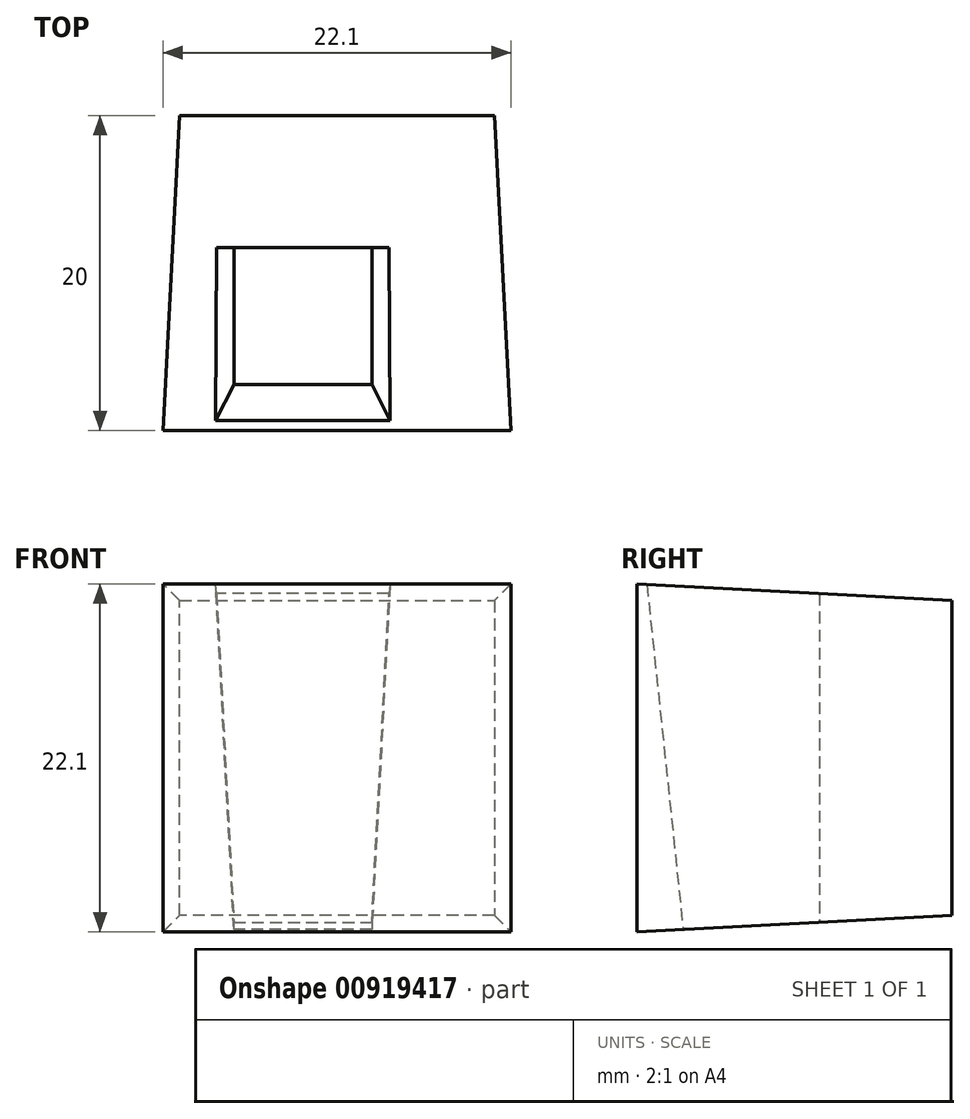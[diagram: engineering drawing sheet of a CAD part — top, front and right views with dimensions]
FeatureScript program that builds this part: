
annotation { "Feature Type Name" : "Feature", "Feature Type Description" : "" }
export const myFeature = defineFeature(function(context is Context, id is Id, definition is map)
    precondition{}
    {
        {
            var Q0;
            Q0=qCreatedBy(makeId("Front.planeOp"),FACE);
            var sketch = newSketch(context, id + "F0", { "sketchPlane" : qUnion([Q0])});
            skLineSegment(sketch, "E0.bottom", {"start": v(-10, 10) * mm, "end": v(10, 10) * mm});
            skLineSegment(sketch, "E0.top", {"start": v(-10, -10) * mm, "end": v(10, -10) * mm});
            skLineSegment(sketch, "E0.left", {"start": v(-10, 10) * mm, "end": v(-10, -10) * mm});
            skLineSegment(sketch, "E0.right", {"start": v(10, 10) * mm, "end": v(10, -10) * mm});
            skPoint(sketch, "E1", {"position": v(-10, 0) * mm});
            skPoint(sketch, "E2", {"position": v(0, 10) * mm});
            skSolve(sketch);
        }
        {
            var Q0;
            Q0=makeQuery(id+"F0.imprint","IMPRINT",FACE,{"disambiguationData":[TD([[makeQuery(id+"F0.imprint","IMPRINT",EDGE,{"derivedFrom":sQuery(id+"F0.wireOp",EDGE,"E0.bottom")}),-1.0]])]});
            extrude(context, id + "F1", {"entities" : qUnion([Q0]), "depth" : 20 * mm, "offsetDistance" : 25.4 * mm, "hasDraft" : true, "draftAngle" : 3 * degree});
        }
        {
            var Q0;
            Q0=makeQuery(id+"F1.opExtrude","SWEPT_FACE",FACE,{"disambiguationData":[OSD([sQuery(id+"F0.wireOp",EDGE,"E0.top")])]});
            var sketch = newSketch(context, id + "F2", { "sketchPlane" : qUnion([Q0])});
            skLineSegment(sketch, "E3.bottom", {"start": v(2.2, 8.93) * mm, "end": v(-6.55, 8.93) * mm});
            skLineSegment(sketch, "E3.top", {"start": v(2.2, 17.61) * mm, "end": v(-6.55, 17.61) * mm});
            skLineSegment(sketch, "E3.left", {"start": v(2.2, 8.93) * mm, "end": v(2.2, 17.61) * mm});
            skLineSegment(sketch, "E3.right", {"start": v(-6.55, 8.93) * mm, "end": v(-6.55, 17.61) * mm});
            skPoint(sketch, "E3.middle", {"position": v(-2.17, 13.27) * mm});
            skSolve(sketch);
        }
        {
            var Q0;
            Q0=makeQuery(id+"F2.imprint","IMPRINT",FACE,{"disambiguationData":[TD([[makeQuery(id+"F2.imprint","IMPRINT",EDGE,{"derivedFrom":sQuery(id+"F2.wireOp",EDGE,"E3.bottom")}),-1.0]])]});
            extrude(context, id + "F3", {"entities" : qUnion([Q0]), "operationType" : NewBodyOperationType.REMOVE, "endBound" : BoundingType.THROUGH_ALL, "oppositeDirection" : true, "depth" : 10 * mm, "offsetDistance" : 25.4 * mm, "hasDraft" : true, "draftAngle" : 3 * degree});
        }
    });
